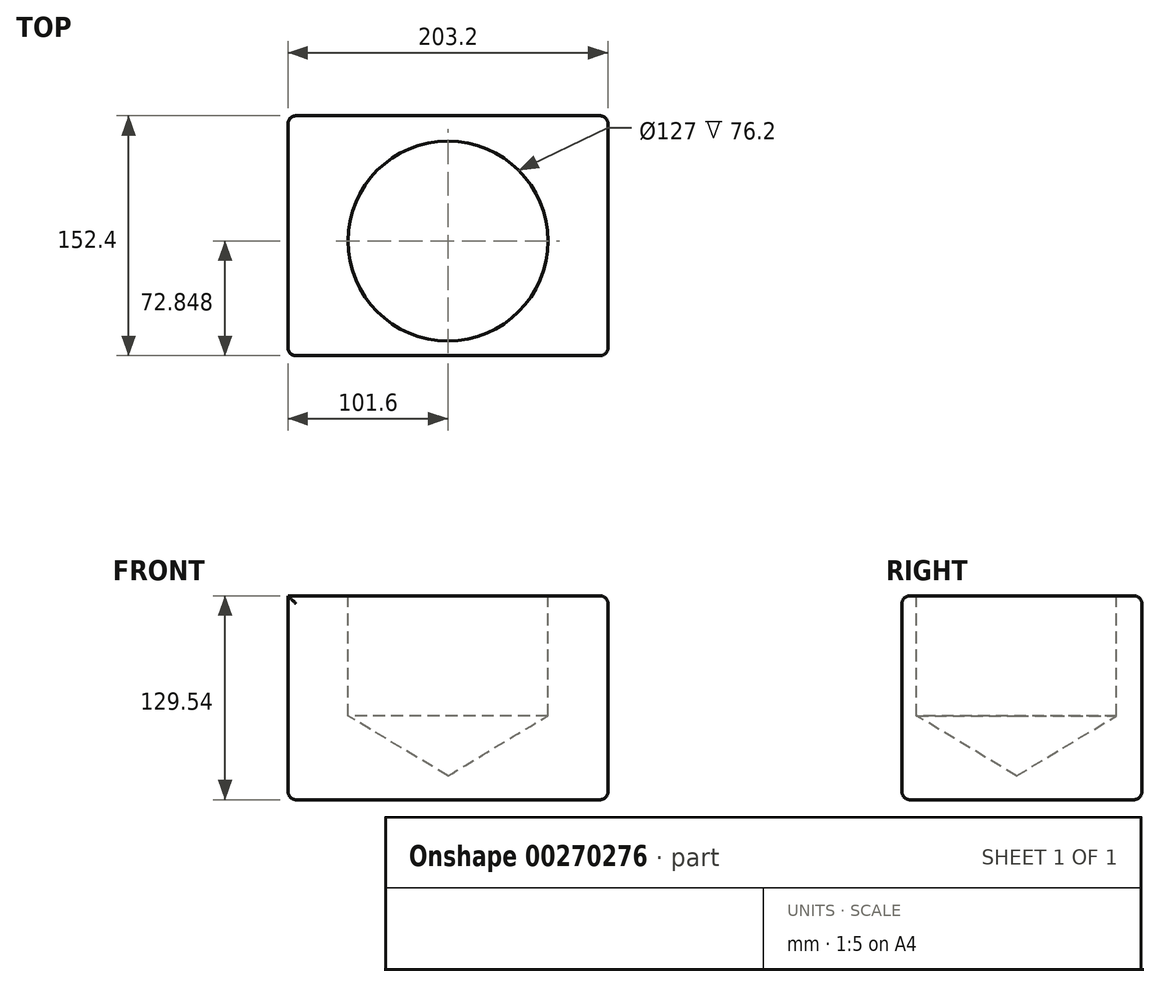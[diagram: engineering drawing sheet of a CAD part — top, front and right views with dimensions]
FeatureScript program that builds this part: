
annotation { "Feature Type Name" : "Feature", "Feature Type Description" : "" }
export const myFeature = defineFeature(function(context is Context, id is Id, definition is map)
    precondition{}
    {
        {
            var Q0;
            Q0=qCreatedBy(makeId("Top.planeOp"),FACE);
            var sketch = newSketch(context, id + "F0", { "sketchPlane" : qUnion([Q0])});
            skEllipse(sketch, "E0", {"center": v(0, -3.35) * mm, "majorRadius": 46.05 * mm, "minorRadius": 34.06 * mm, "majorAxis": v(0, 1)});
            skSolve(sketch);
        }
        {
            var Q0;
            Q0=qCreatedBy(makeId("Front.planeOp"),FACE);
            var sketch = newSketch(context, id + "F1", { "sketchPlane" : qUnion([Q0])});
            skLineSegment(sketch, "E1.bottom", {"start": v(101.6, 0) * mm, "end": v(-101.6, 0) * mm});
            skLineSegment(sketch, "E1.top", {"start": v(101.6, -127) * mm, "end": v(-101.6, -127) * mm});
            skLineSegment(sketch, "E1.left", {"start": v(101.6, 0) * mm, "end": v(101.6, -127) * mm});
            skLineSegment(sketch, "E1.right", {"start": v(-101.6, 0) * mm, "end": v(-101.6, -127) * mm});
            skPoint(sketch, "E1.middle", {"position": v(0, -63.5) * mm});
            skSolve(sketch);
        }
        {
            var Q0;
            Q0=makeQuery(id+"F1.imprint","IMPRINT",FACE,{"disambiguationData":[TD([[makeQuery(id+"F1.imprint","IMPRINT",EDGE,{"derivedFrom":sQuery(id+"F1.wireOp",EDGE,"E1.bottom")}),1.0]])]});
            extrude(context, id + "F2", {"entities" : qUnion([Q0]), "endBound" : BoundingType.SYMMETRIC, "depth" : 152.4 * mm});
        }
        {
            var Q0;
            Q0=sQuery(id+"F0.wireOp",VERTEX,"E0.center");
            var Q1;
            Q1=makeQuery(id+"F2.opExtrude","SWEPT_BODY",BODY,{"disambiguationData":[OSD([sQuery(id+"F1.wireOp",EDGE,"E1.bottom"),sQuery(id+"F1.wireOp",EDGE,"E1.top"),sQuery(id+"F1.wireOp",EDGE,"E1.left"),sQuery(id+"F1.wireOp",EDGE,"E1.right")])]});
            hole(context, id + "F3", {"style" : HoleStyle.SIMPLE, "endStyle" : HoleEndStyle.BLIND, "holeDiameter" : 127 * mm, "holeDepth" : 76.2 * mm, "tappedDepth" : 12.7 * mm, "tapClearance" : 3, "locations" : qUnion([Q0]), "scope" : qUnion([Q1])});
        }
        {
            var Q0;
            Q0=makeQuery(id+"F2.opExtrude","SWEPT_FACE",FACE,{"disambiguationData":[OSD([sQuery(id+"F1.wireOp",EDGE,"E1.top")])]});
            extrude(context, id + "F4", {"entities" : qUnion([Q0]), "operationType" : NewBodyOperationType.ADD, "depth" : 2.54 * mm});
        }
        {
            var Q0;
            Q0=makeQuery(id+"F2.opExtrude","CAP_EDGE",EDGE,{"disambiguationData":[OSD([sQuery(id+"F1.wireOp",EDGE,"E1.bottom")])],"isStart":true});
            var Q1;
            Q1=makeQuery(id+"F2.opExtrude","SWEPT_EDGE",EDGE,{"disambiguationData":[OSD([sQuery(id+"F1.wireOp",EDGE,"E1.bottom"),sQuery(id+"F1.wireOp",EDGE,"E1.left")])]});
            var Q2;
            Q2=makeQuery(id+"F4.opExtrude","CAP_EDGE",EDGE,{"disambiguationData":[OSD([sQuery(id+"F1.wireOp",EDGE,"E1.top"),sQuery(id+"F1.wireOp",EDGE,"E1.left")])],"isStart":false});
            var Q3;
            Q3=makeQuery(id+"F2.opExtrude","CAP_EDGE",EDGE,{"disambiguationData":[OSD([sQuery(id+"F1.wireOp",EDGE,"E1.bottom")])],"isStart":false});
            var Q4;
            Q4=makeQuery(id+"F3.hole-0.boolean.opBoolean","COPY",EDGE,{"derivedFrom":makeQuery(id+"F3.hole-0.opRevolve","SWEPT_EDGE",EDGE,{"disambiguationData":[OSD([sQuery(id+"F3.hole-0.sketch.wireOp",EDGE,"core_line_2"),sQuery(id+"F3.hole-0.sketch.wireOp",EDGE,"core_line_3")])]})});
            var Q5;
            {var subQ0=sQuery(id+"F1.wireOp",EDGE,"E1.top");Q5=makeQuery(id+"F4.opExtrude","CAP_EDGE",EDGE,{"disambiguationData":[OSD([subQ0]),TDD([makeQuery(id+"F2.opExtrude","CAP_EDGE",EDGE,{"disambiguationData":[OSD([subQ0])],"isStart":false})])],"isStart":false});}
            var Q6;
            Q6=makeQuery(id+"F3.hole-0.boolean.opBoolean","COPY",EDGE,{"derivedFrom":makeQuery(id+"F3.hole-0.opRevolve","SWEPT_EDGE",EDGE,{"disambiguationData":[OSD([sQuery(id+"F3.hole-0.sketch.wireOp",EDGE,"core_line_1"),sQuery(id+"F3.hole-0.sketch.wireOp",EDGE,"core_line_2")])]})});
            var Q7;
            {var subQ0=sQuery(id+"F1.wireOp",EDGE,"E1.right");var subQ1=sQuery(id+"F1.wireOp",EDGE,"E1.top");Q7=makeQuery(id+"F4.boolean.opBoolean","MERGE",EDGE,{"derivedFrom":[makeQuery(id+"F2.opExtrude","CAP_EDGE",EDGE,{"disambiguationData":[OSD([subQ0])],"isStart":false}),makeQuery(id+"F4.opExtrude","SWEPT_EDGE",EDGE,{"disambiguationData":[OSD([subQ1,subQ0]),TDD([makeQuery(id+"F2.opExtrude","CAP_VERTEX",VERTEX,{"disambiguationData":[OSD([subQ1,subQ0])],"isStart":false})])]})]});}
            var Q8;
            {var subQ0=sQuery(id+"F1.wireOp",EDGE,"E1.left");var subQ1=sQuery(id+"F1.wireOp",EDGE,"E1.top");Q8=makeQuery(id+"F4.boolean.opBoolean","MERGE",EDGE,{"derivedFrom":[makeQuery(id+"F2.opExtrude","CAP_EDGE",EDGE,{"disambiguationData":[OSD([subQ0])],"isStart":false}),makeQuery(id+"F4.opExtrude","SWEPT_EDGE",EDGE,{"disambiguationData":[OSD([subQ1,subQ0]),TDD([makeQuery(id+"F2.opExtrude","CAP_VERTEX",VERTEX,{"disambiguationData":[OSD([subQ1,subQ0])],"isStart":false})])]})]});}
            var Q9;
            {var subQ0=sQuery(id+"F1.wireOp",EDGE,"E1.left");var subQ1=sQuery(id+"F1.wireOp",EDGE,"E1.top");Q9=makeQuery(id+"F4.boolean.opBoolean","MERGE",EDGE,{"derivedFrom":[makeQuery(id+"F2.opExtrude","CAP_EDGE",EDGE,{"disambiguationData":[OSD([subQ0])],"isStart":true}),makeQuery(id+"F4.opExtrude","SWEPT_EDGE",EDGE,{"disambiguationData":[OSD([subQ1,subQ0]),TDD([makeQuery(id+"F2.opExtrude","CAP_VERTEX",VERTEX,{"disambiguationData":[OSD([subQ1,subQ0])],"isStart":true})])]})]});}
            var Q10;
            {var subQ0=sQuery(id+"F1.wireOp",EDGE,"E1.right");var subQ1=sQuery(id+"F1.wireOp",EDGE,"E1.top");Q10=makeQuery(id+"F4.boolean.opBoolean","MERGE",EDGE,{"derivedFrom":[makeQuery(id+"F2.opExtrude","CAP_EDGE",EDGE,{"disambiguationData":[OSD([subQ0])],"isStart":true}),makeQuery(id+"F4.opExtrude","SWEPT_EDGE",EDGE,{"disambiguationData":[OSD([subQ1,subQ0]),TDD([makeQuery(id+"F2.opExtrude","CAP_VERTEX",VERTEX,{"disambiguationData":[OSD([subQ1,subQ0])],"isStart":true})])]})]});}
            var Q11;
            {var subQ0=sQuery(id+"F1.wireOp",EDGE,"E1.top");Q11=makeQuery(id+"F4.opExtrude","CAP_EDGE",EDGE,{"disambiguationData":[OSD([subQ0]),TDD([makeQuery(id+"F2.opExtrude","CAP_EDGE",EDGE,{"disambiguationData":[OSD([subQ0])],"isStart":true})])],"isStart":false});}
            var Q12;
            Q12=makeQuery(id+"F4.opExtrude","CAP_EDGE",EDGE,{"disambiguationData":[OSD([sQuery(id+"F1.wireOp",EDGE,"E1.top"),sQuery(id+"F1.wireOp",EDGE,"E1.right")])],"isStart":false});
            fillet(context, id + "F5", {"entities" : qUnion([Q0, Q1, Q2, Q3, Q4, Q5, Q6, Q7, Q8, Q9, Q10, Q11, Q12]), "radius" : 5.08 * mm, "tangentPropagation" : true, "allowEdgeOverflow" : false});
        }
    });
